FCSTD DOCUMENT  (FreeCAD 1.0R39319 (Git))
Label: session3_spreadsheet_exercise
License: All rights reserved
LicenseURL: https://en.wikipedia.org/wiki/All_rights_reserved
objects: Spreadsheet::Sheet×1, Sketcher::SketchObject×1, PartDesign::Body×1
note: 3 computed .brp shape members not serialized (recipe doc carries the construction recipe); baked Part::Feature solids carry a one-line shape summary decoded from their .brp

FEATURE [Spreadsheet::Sheet] Spreadsheet
  cells = A1='centre_inner_circle_dia; B1(centre_inner_circle_dia)=56; A2='centre_outer_circle_dia; B2(centre_outer_circle_dia)=88; A3='top_circle_dia; B3(top_circle_dia)=44; A4='side_circle_dia; B4(side_circle_dia)=36; A5='top_arc_rad; B5(top_arc_rad)=44; A6='side_arc_rad; B6(side_arc_rad)=40; A7='ydist_centre_top_circle; B7(ydist_centre_top_circle)=176; A8='diagonal_arc_rad; B8(diagonal_arc_rad)=88; A9='lower_arc_rad; B9(lower_arc_rad)=32; A10='slot_angle; B10(slot_angle)=40; A11='slot_rad; B11(slot_rad)=22; A12='outer_slot_rad; B12(outer_slot_rad)=44; A13='ydist_centre_bottom; B13(ydist_centre_bottom)=120; A14='arc_rad; B14(arc_rad)=70; A15='xdist_centre_side_circle; B15(xdist_centre_side_circle)=96; A16='ydist_centre_side_circle; B16(ydist_centre_side_circle)=38
FEATURE [Sketcher::SketchObject] Sketch
  ArcFitTolerance = 1e-06
  AttachmentSupport = -> [XY_Plane]
  FullyConstrained = true
  MakeInternals = false
  MapMode = 5
  expr: Constraints[11] = <<Spreadsheet>>.top_arc_rad
  expr: Constraints[15] = <<Spreadsheet>>.arc_rad
  expr: Constraints[16] = <<Spreadsheet>>.lower_arc_rad
  expr: Constraints[23] = <<Spreadsheet>>.slot_angle
  expr: Constraints[24] = <<Spreadsheet>>.ydist_centre_bottom
  expr: Constraints[25] = <<Spreadsheet>>.outer_slot_rad
  expr: Constraints[2] = <<Spreadsheet>>.centre_inner_circle_dia
  expr: Constraints[33] = <<Spreadsheet>>.slot_rad
  expr: Constraints[37] = <<Spreadsheet>>.diagonal_arc_rad
  expr: Constraints[38] = <<Spreadsheet>>.side_arc_rad
  expr: Constraints[39] = <<Spreadsheet>>.lower_arc_rad
  expr: Constraints[3] = <<Spreadsheet>>.centre_outer_circle_dia
  expr: Constraints[5] = <<Spreadsheet>>.top_circle_dia
  expr: Constraints[6] = <<Spreadsheet>>.ydist_centre_top_circle
  expr: Constraints[7] = <<Spreadsheet>>.side_circle_dia
  expr: Constraints[8] = <<Spreadsheet>>.ydist_centre_side_circle
  expr: Constraints[9] = <<Spreadsheet>>.xdist_centre_side_circle
  sketch-geometry (19):
    g0: Circle CenterX=0 CenterY=0 CenterZ=0 NormalX=0 NormalY=0 NormalZ=1 AngleXU=0 Radius=44
    g1: Circle CenterX=0 CenterY=0 CenterZ=0 NormalX=0 NormalY=0 NormalZ=1 AngleXU=0 Radius=28
    g2: Circle CenterX=0 CenterY=176 CenterZ=0 NormalX=0 NormalY=0 NormalZ=1 AngleXU=0 Radius=22
    g3: Circle CenterX=96 CenterY=38 CenterZ=0 NormalX=0 NormalY=0 NormalZ=1 AngleXU=0 Radius=18
    g4: ArcOfCircle CenterX=0 CenterY=176 CenterZ=0 NormalX=0 NormalY=0 NormalZ=1 AngleXU=0 Radius=44 StartAngle=6.1699 EndAngle=9.27651
    g5: LineSegment StartX=-43.5172 StartY=182.5 StartZ=0 EndX=-69.232 EndY=10.3409 EndZ=0
    g6: ArcOfCircle CenterX=0 CenterY=0 CenterZ=0 NormalX=0 NormalY=0 NormalZ=1 AngleXU=0 Radius=70 StartAngle=2.99332 EndAngle=4.03194
    g7: ArcOfCircle CenterX=-64.1728 CenterY=-79.2833 CenterZ=0 NormalX=0 NormalY=0 NormalZ=1 AngleXU=0 Radius=32 StartAngle=5.71779 EndAngle=7.17353
    g8: ArcOfCircle CenterX=0 CenterY=-120 CenterZ=0 NormalX=0 NormalY=0 NormalZ=1 AngleXU=0 Radius=44 StartAngle=2.5762 EndAngle=4.99487
    g9: ArcOfCircle CenterX=80.9716 CenterY=-96.4982 CenterZ=0 NormalX=0 NormalY=0 NormalZ=1 AngleXU=0 Radius=44 StartAngle=4.99487 EndAngle=7.33781
    g10: LineSegment StartX=12.2647 StartY=-162.256 StartZ=0 EndX=93.2363 EndY=-138.754 EndZ=0
    g11: LineSegment [constr] StartX=0 StartY=0 StartZ=0 EndX=104.596 EndY=-124.652 EndZ=0
    g12: ArcOfCircle CenterX=0 CenterY=-120 CenterZ=0 NormalX=0 NormalY=0 NormalZ=1 AngleXU=0 Radius=22 StartAngle=1.85328 EndAngle=4.99487
    g13: ArcOfCircle CenterX=80.9716 CenterY=-96.4982 CenterZ=0 NormalX=0 NormalY=0 NormalZ=1 AngleXU=0 Radius=22 StartAngle=4.99487 EndAngle=8.13647
    g14: LineSegment StartX=-6.13237 StartY=-98.872 StartZ=0 EndX=74.8392 EndY=-75.3701 EndZ=0
    g15: LineSegment StartX=6.13237 StartY=-141.128 StartZ=0 EndX=87.104 EndY=-117.626 EndZ=0
    g16: ArcOfCircle CenterX=131.154 CenterY=161.078 CenterZ=0 NormalX=0 NormalY=0 NormalZ=1 AngleXU=0 Radius=88 StartAngle=3.02831 EndAngle=4.43417
    g17: ArcOfCircle CenterX=96 CenterY=38 CenterZ=0 NormalX=0 NormalY=0 NormalZ=1 AngleXU=0 Radius=40 StartAngle=5.02995 EndAngle=7.57577
    g18: ArcOfCircle CenterX=118.482 CenterY=-30.4 CenterZ=0 NormalX=0 NormalY=0 NormalZ=1 AngleXU=0 Radius=32 StartAngle=1.88836 EndAngle=4.19621
  constraints (47):
    c: Coincident(g0,g-1)
    c: Coincident(g1,g0)
    c: Diameter(g1) = 56
    c: Diameter(g0) = 88
    c: PointOnObject(g2,g-2)
    c: Diameter(g2) = 44
    c: DistanceY(g-1,g2) = 176
    c: Diameter(g3) = 36
    c: Distance(g3,g-1) = 38
    c: DistanceX(g0,g3) = 96
    c: Coincident(g4,g2)
    c: Radius(g4) = 44
    c: Tangent(g5,g4) = -1.5708
    c: Tangent(g6,g7) = 1.5708
    c: Tangent(g6,g5) = -1.5708
    c: Radius(g6) = 70
    c: Radius(g7) = 32
    c: Tangent(g8,g10) = -1.5708
    c: Tangent(g9,g10) = -1.5708
    c: Equal(g8,g9)
    c: PointOnObject(g8,g-2)
    c: Coincident(g11,g0)
    c: PointOnObject(g9,g11)
    c: Angle(g-2,g11) = 0.698132
    c: DistanceY(g8,g0) = 120
    c: Radius(g9) = 44
    c: Tangent(g12,g14) = 1.5708
    c: Tangent(g12,g15) = -1.5708
    c: Tangent(g13,g14) = 1.5708
    c: Tangent(g13,g15) = -1.5708
    c: Equal(g12,g13)
    c: Coincident(g12,g8)
    c: PointOnObject(g13,g11)
    c: Radius(g13) = 22
    c: Tangent(g16,g17) = 1.5708
    c: Tangent(g17,g18) = 1.5708
    c: Tangent(g4,g16) = 1.5708
    c: Radius(g16) = 88
    c: Radius(g17) = 40
    c: Radius(g18) = 32
    c: Coincident(g17,g3)
    c: Tangent(g8,g7) = 1.5708
    c: Tangent(g9,g18) = 1.5708
    c: Parallel(g10,g15)
    c: Coincident(g6,g0)
    c: Horizontal(g0,g17)
    c: Block(g11)
FEATURE [PartDesign::Body] Body
  AllowCompound = false
  Group = -> [Sketch]
  Origin = -> Origin
